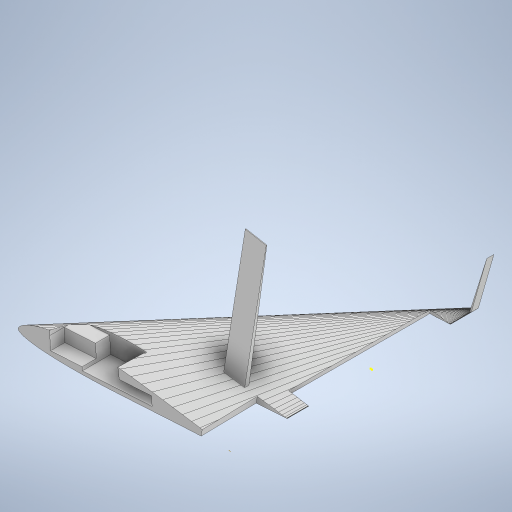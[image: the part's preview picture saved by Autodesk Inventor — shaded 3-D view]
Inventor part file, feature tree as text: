
AUTODESK INVENTOR PART (.ipt)
format: ipt  version: 2023 (Build 270158000, 158)  size: 915,968 bytes
history: native  units: mm
features: sketch x12, extrude x8, other x4, loft x2
ambient origin geometry x8: Origin, YZ Plane, XZ Plane, XY Plane, X Axis, Y Axis, Z Axis, Center Point
bodies: Body1 (feature_tree), Body2 (feature_tree)
feature tree (26):
  sketch  "Szkic1"
  other  "Płaszczyzna konstrukcyjna2"
  loft  "Wyciągnięcie złożone2"
  other  "Płaszczyzna konstrukcyjna3"
  sketch  "Szkic7"
  extrude  "Wyciągnięcie proste2"  Depth=31.159588mm
  extrude  "Wyciągnięcie proste3"  Depth=1.516701mm
  extrude  "Wyciągnięcie proste4"  Depth=30.924079mm
  sketch  "Szkic11"
  other  "Płaszczyzna konstrukcyjna4"
  loft  "Wyciągnięcie złożone3"
  other  "Płaszczyzna konstrukcyjna5"
  sketch  "Szkic13"
  extrude  "Wyciągnięcie proste5"  Depth=30.873012mm
  sketch  "Szkic15"
  extrude  "Wyciągnięcie proste6"  Depth=29.561471mm
  extrude  "Wyciągnięcie proste7"  Depth=0.447545mm
  extrude  "Wyciągnięcie proste8"  Depth=29.600828mm
  extrude  "Wyciągnięcie proste9"  Depth=0.338663mm
  sketch  "Szkic6"
  sketch  "Szkic8"
  sketch  "Szkic9"
  sketch  "Szkic10"
  sketch  "Szkic12"
  sketch  "Szkic14"
  sketch  "Szkic16"
